# Revit family: Power-MouldedCaseDevices-GEWISS-97MSS-SWITCH_DISCONNECTOR_160
name_source: partatom
category: Apparecchi elettrici
revit_build: Autodesk Revit 2016 (Build: 20161004_0715(x64)
units: mm (PartAtom-declared; Revit-internal decimal feet)

## family parameters
Condiviso = No
Host = Muro
Mantenere orientamento annotazione = Sì
Numero OmniClass = 23.80.50.00
Punto di calcolo locali = Sì
Quota connettore circolare = Usa diametro
Sempre verticale = Sì
Taglio con vuoti quando caricato = No
Tipo di parte = Normale
Titolo OmniClass = Terminals for Power Supply

## types (2) — shared parameters
Catalogue = POWER
Catalogue Range = 97 MSS
GW - Codice Electrocod = 150
IDF = 1ba8dad1-0f5a-4405-9d0f-1eb80bc87f7b
IDT = ae166635-42b5-4973-98c0-4df5846345b0
Immagine tipo = GW97728.jpg
Label = MSS 160
No. Chorus modules = 8
No. of modules EN 50022 = 8
Produttore = GEWISS S.p.A.
Rated current (In) = 160A
Rated current: = 160A
Rated voltage = 400V
SEO = Disconnector
Technical sheet = https://www.gewiss.com
URL = https://www.gewiss.com
Version file RFA = 18.0

## per-type parameters (varying)
| type | Descrizione | EAN code | Modello | No. of poles | Number of poles |
| GW97728 - SWITCH DISCONNECTOR MSS 160 4P 160A | SWITCH DISCONNECTOR MSS 160 4P 160A | 8011564211483 | GW97728 | 4P | 4P |
| GW97727 - SWITCH DISCONNECTOR MSS 160 3P 160A | SWITCH DISCONNECTOR MSS 160 3P 160A | 8011564211476 | GW97727 | 3P | 3P |
